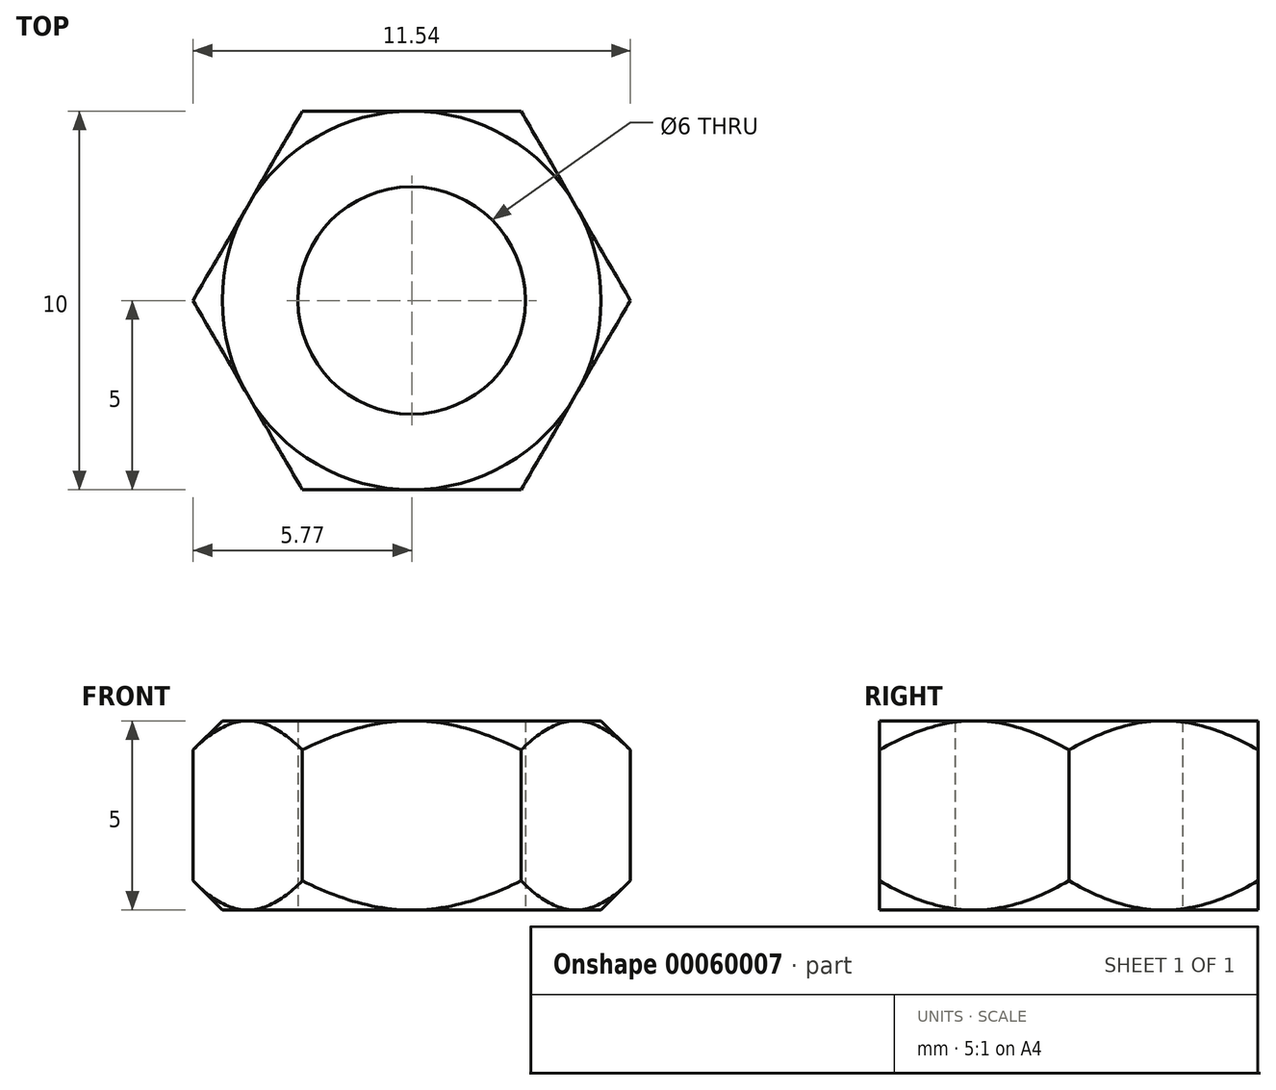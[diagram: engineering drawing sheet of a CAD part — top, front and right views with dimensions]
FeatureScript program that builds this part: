
annotation { "Feature Type Name" : "Feature", "Feature Type Description" : "" }
export const myFeature = defineFeature(function(context is Context, id is Id, definition is map)
    precondition{}
    {
        {
            var Q0;
            Q0=qCreatedBy(makeId("Top.planeOp"),FACE);
            var sketch = newSketch(context, id + "F0", { "sketchPlane" : qUnion([Q0])});
            skCircle(sketch, "E0.cCircle", {"center": v(0, 0) * mm, "radius": 5 * mm, "construction": true});
            skLineSegment(sketch, "E0.0", {"start": v(-2.89, 5) * mm, "end": v(2.89, 5) * mm});
            skLineSegment(sketch, "E0.1", {"start": v(2.89, 5) * mm, "end": v(5.77, 0) * mm});
            skLineSegment(sketch, "E0.2", {"start": v(5.77, 0) * mm, "end": v(2.89, -5) * mm});
            skLineSegment(sketch, "E0.3", {"start": v(2.89, -5) * mm, "end": v(-2.89, -5) * mm});
            skLineSegment(sketch, "E0.4", {"start": v(-2.89, -5) * mm, "end": v(-5.77, 0) * mm});
            skLineSegment(sketch, "E0.5", {"start": v(-5.77, 0) * mm, "end": v(-2.89, 5) * mm});
            skPoint(sketch, "E0.0.midPoint", {"position": v(0, 5) * mm});
            skCircle(sketch, "E1", {"center": v(0, 0) * mm, "radius": 3 * mm});
            skSolve(sketch);
        }
        {
            var Q0;
            Q0=makeQuery(id+"F0.imprint","IMPRINT",FACE,{"disambiguationData":[TD([[makeQuery(id+"F0.imprint","IMPRINT",EDGE,{"derivedFrom":sQuery(id+"F0.wireOp",EDGE,"E0.0")}),-1.0]])]});
            extrude(context, id + "F1", {"entities" : qUnion([Q0]), "endBound" : BoundingType.SYMMETRIC, "depth" : 5 * mm});
        }
        {
            var Q0;
            Q0=qCreatedBy(makeId("Front.planeOp"),FACE);
            var sketch = newSketch(context, id + "F2", { "sketchPlane" : qUnion([Q0])});
            skLineSegment(sketch, "E2", {"start": v(-5.77, 1.73) * mm, "end": v(-5, 2.5) * mm});
            skLineSegment(sketch, "E3", {"start": v(-5, 2.5) * mm, "end": v(-5.77, 2.5) * mm});
            skLineSegment(sketch, "E4", {"start": v(-5.77, 2.5) * mm, "end": v(-5.77, 1.73) * mm});
            skLineSegment(sketch, "E5", {"start": v(0, 3.4) * mm, "end": v(0, -3.52) * mm, "construction": true});
            skLineSegment(sketch, "E6", {"start": v(-5.77, -1.73) * mm, "end": v(-5.77, -2.5) * mm});
            skLineSegment(sketch, "E7", {"start": v(-5.77, -2.5) * mm, "end": v(-5, -2.5) * mm});
            skLineSegment(sketch, "E8", {"start": v(-5, -2.5) * mm, "end": v(-5.77, -1.73) * mm});
            skSolve(sketch);
        }
        {
            var Q0;
            Q0 = qSketchRegion(id + "F2", true);
            var Q1;
            Q1=sQuery(id+"F2.wireOp",EDGE,"E5");
            revolve(context, id + "F3", {"operationType" : NewBodyOperationType.REMOVE, "entities" : qUnion([Q0]), "axis" : qUnion([Q1]), "revolveType" : RevolveType.FULL, "oppositeDirection" : true});
        }
    });
